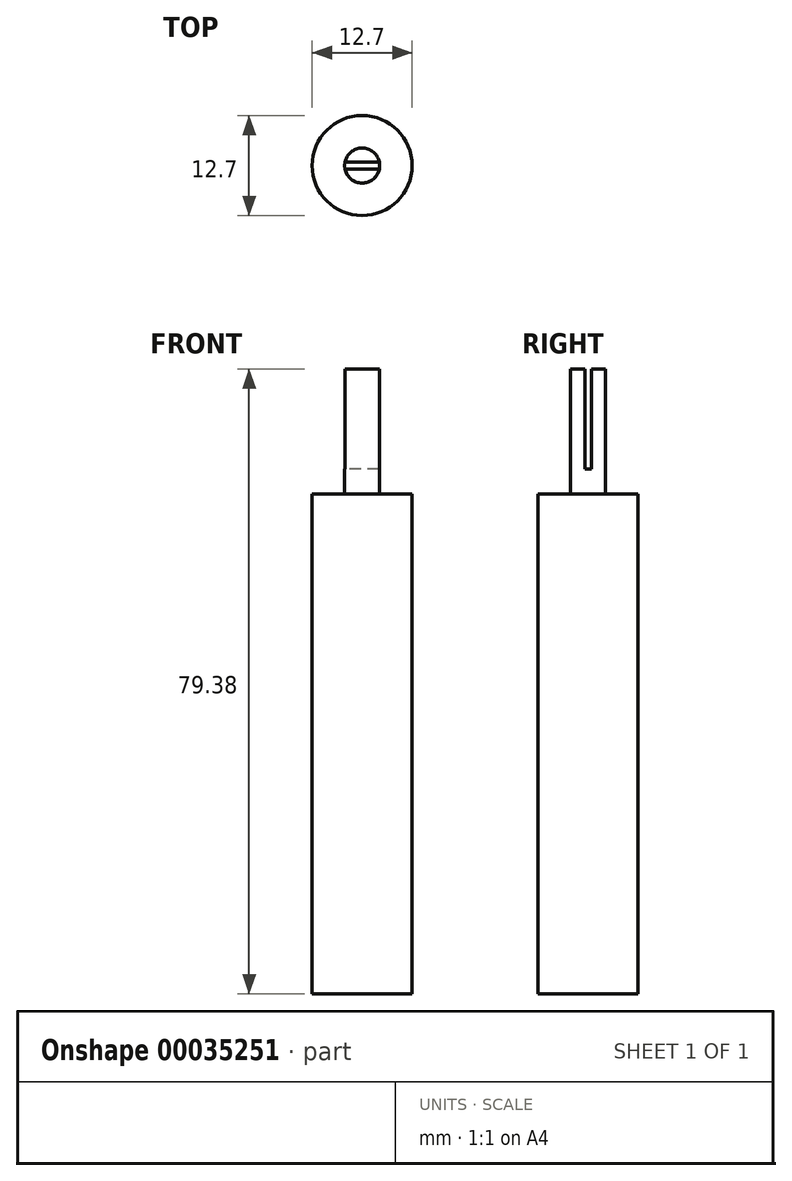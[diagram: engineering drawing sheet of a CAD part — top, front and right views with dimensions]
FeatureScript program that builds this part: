
annotation { "Feature Type Name" : "Feature", "Feature Type Description" : "" }
export const myFeature = defineFeature(function(context is Context, id is Id, definition is map)
    precondition{}
    {
        {
            var Q0;
            Q0=qCreatedBy(makeId("Top.planeOp"),FACE);
            var sketch = newSketch(context, id + "F0", { "sketchPlane" : qUnion([Q0])});
            skCircle(sketch, "E0", {"center": v(0, 0) * mm, "radius": 6.35 * mm});
            skSolve(sketch);
        }
        {
            var Q0;
            Q0=makeQuery(id+"F0.imprint","IMPRINT",FACE,{"disambiguationData":[TD([[makeQuery(id+"F0.imprint","IMPRINT",EDGE,{"derivedFrom":sQuery(id+"F0.wireOp",EDGE,"E0")}),1.0]])]});
            extrude(context, id + "F1", {"entities" : qUnion([Q0]), "depth" : 63.5 * mm});
        }
        {
            var Q0;
            Q0=makeQuery(id+"F1.opExtrude","CAP_FACE",FACE,{"disambiguationData":[OSD([sQuery(id+"F0.wireOp",EDGE,"E0")])],"isStart":false});
            var sketch = newSketch(context, id + "F2", { "sketchPlane" : qUnion([Q0])});
            skCircle(sketch, "E1", {"center": v(0, 0) * mm, "radius": 2.22 * mm});
            skSolve(sketch);
        }
        {
            var Q0;
            Q0=makeQuery(id+"F2.imprint","IMPRINT",FACE,{"disambiguationData":[TD([[makeQuery(id+"F2.imprint","IMPRINT",EDGE,{"derivedFrom":sQuery(id+"F2.wireOp",EDGE,"E1")}),1.0]])]});
            extrude(context, id + "F3", {"entities" : qUnion([Q0]), "operationType" : NewBodyOperationType.ADD, "depth" : 3.17 * mm});
        }
        {
            var Q0;
            Q0=makeQuery(id+"F3.opExtrude","CAP_FACE",FACE,{"disambiguationData":[OSD([sQuery(id+"F2.wireOp",EDGE,"E1")])],"isStart":false});
            var sketch = newSketch(context, id + "F4", { "sketchPlane" : qUnion([Q0])});
            skLineSegment(sketch, "E2.rect.bottom", {"start": v(2.18, -0.42) * mm, "end": v(-2.18, -0.42) * mm});
            skLineSegment(sketch, "E2.rect.top", {"start": v(2.18, 0.42) * mm, "end": v(-2.18, 0.42) * mm});
            skPoint(sketch, "E2.rect.middle", {"position": v(0, 0) * mm});
            skSolve(sketch);
        }
        {
            var Q0;
            {var subQ1=sQuery(id+"F4.wireOp",EDGE,"E2.rect.bottom");Q0=makeQuery(id+"F4.imprint","IMPRINT",FACE,{"disambiguationData":[TD([[makeQuery(id+"F4.imprint","IMPRINT",EDGE,{"derivedFrom":subQ1}),1.0]])]});}
            var Q1;
            {var subQ1=sQuery(id+"F4.wireOp",EDGE,"E2.rect.top");Q1=makeQuery(id+"F4.imprint","IMPRINT",FACE,{"disambiguationData":[TD([[makeQuery(id+"F4.imprint","IMPRINT",EDGE,{"derivedFrom":subQ1}),-1.0]])]});}
            extrude(context, id + "F5", {"entities" : qUnion([Q0, Q1]), "operationType" : NewBodyOperationType.ADD, "depth" : 12.7 * mm});
        }
    });
